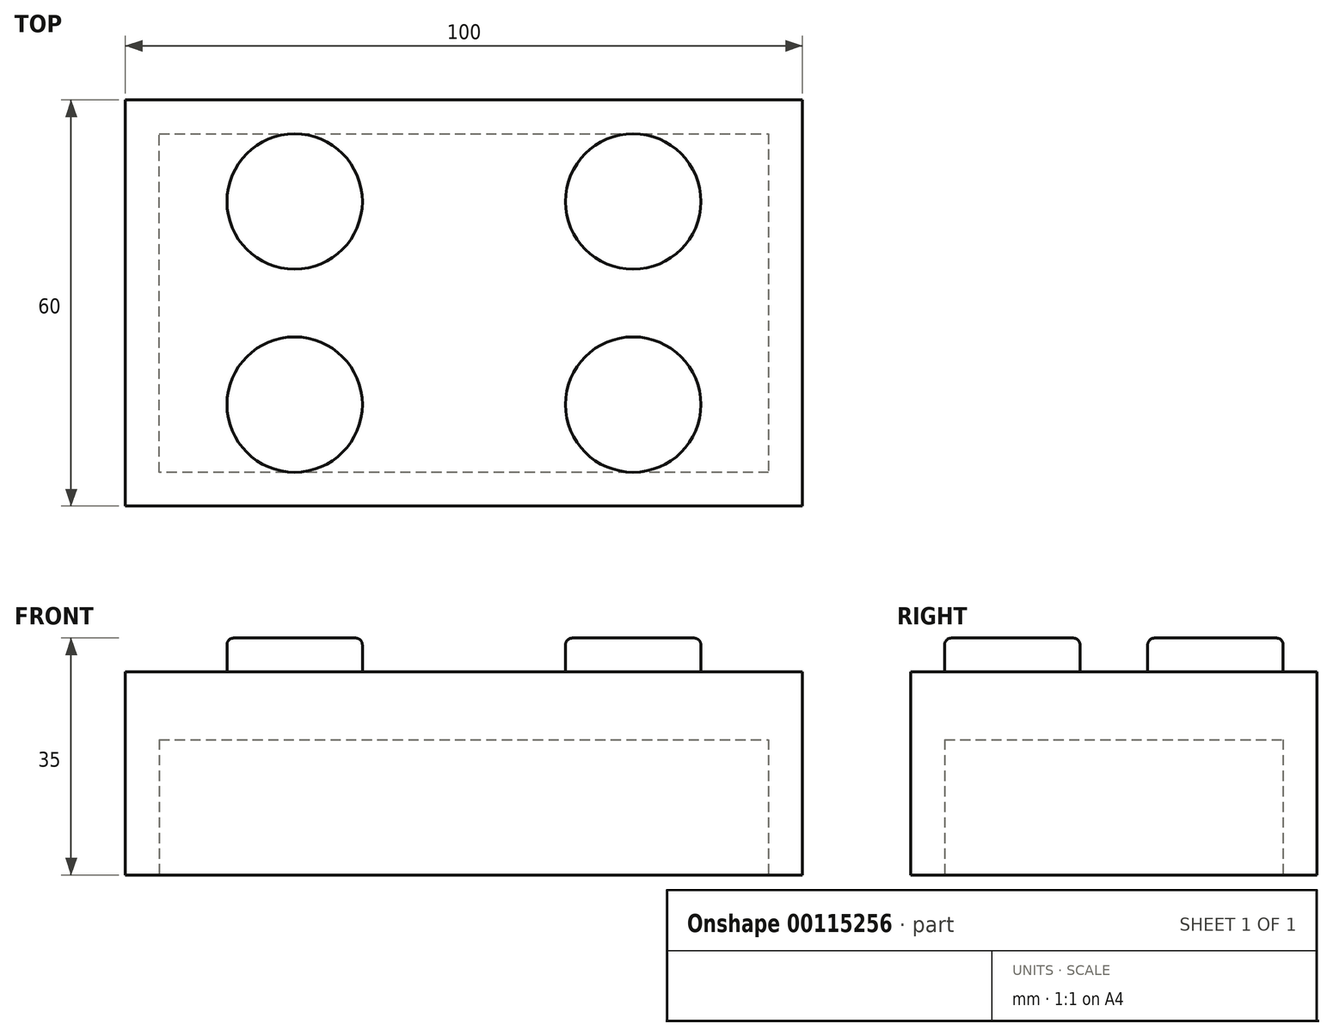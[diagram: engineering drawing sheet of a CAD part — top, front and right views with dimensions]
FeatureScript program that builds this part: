
annotation { "Feature Type Name" : "Feature", "Feature Type Description" : "" }
export const myFeature = defineFeature(function(context is Context, id is Id, definition is map)
    precondition{}
    {
        {
            var Q0;
            Q0=qCreatedBy(makeId("Top.planeOp"),FACE);
            var sketch = newSketch(context, id + "F0", { "sketchPlane" : qUnion([Q0])});
            skLineSegment(sketch, "E0.bottom", {"start": v(-55.04, 76.41) * mm, "end": v(44.96, 76.41) * mm});
            skLineSegment(sketch, "E0.top", {"start": v(-55.04, 16.41) * mm, "end": v(44.96, 16.41) * mm});
            skLineSegment(sketch, "E0.left", {"start": v(-55.04, 76.41) * mm, "end": v(-55.04, 16.41) * mm});
            skLineSegment(sketch, "E0.right", {"start": v(44.96, 76.41) * mm, "end": v(44.96, 16.41) * mm});
            skSolve(sketch);
        }
        {
            var Q0;
            Q0 = qSketchRegion(id + "F0", true);
            extrude(context, id + "F1", {"entities" : qUnion([Q0]), "depth" : 30 * mm});
        }
        {
            var Q0;
            Q0=makeQuery(id+"F1.opExtrude","CAP_FACE",FACE,{"disambiguationData":[OSD([sQuery(id+"F0.wireOp",EDGE,"E0.bottom"),sQuery(id+"F0.wireOp",EDGE,"E0.top"),sQuery(id+"F0.wireOp",EDGE,"E0.left"),sQuery(id+"F0.wireOp",EDGE,"E0.right")])],"isStart":true});
            var sketch = newSketch(context, id + "F2", { "sketchPlane" : qUnion([Q0])});
            skLineSegment(sketch, "E1.0", {"start": v(-50.04, -71.41) * mm, "end": v(39.96, -71.41) * mm});
            skLineSegment(sketch, "E1.1", {"start": v(-50.04, -21.41) * mm, "end": v(-50.04, -71.41) * mm});
            skLineSegment(sketch, "E1.2", {"start": v(39.96, -21.41) * mm, "end": v(-50.04, -21.41) * mm});
            skLineSegment(sketch, "E1.3", {"start": v(39.96, -71.41) * mm, "end": v(39.96, -21.41) * mm});
            skSolve(sketch);
        }
        {
            var Q0;
            Q0=makeQuery(id+"F2.imprint","IMPRINT",FACE,{"disambiguationData":[TD([[makeQuery(id+"F2.imprint","IMPRINT",EDGE,{"derivedFrom":sQuery(id+"F2.wireOp",EDGE,"E1.0")}),1.0]])]});
            extrude(context, id + "F3", {"entities" : qUnion([Q0]), "operationType" : NewBodyOperationType.REMOVE, "oppositeDirection" : true, "depth" : 20 * mm});
        }
        {
            var Q0;
            Q0=makeQuery(id+"F1.opExtrude","CAP_FACE",FACE,{"disambiguationData":[OSD([sQuery(id+"F0.wireOp",EDGE,"E0.bottom"),sQuery(id+"F0.wireOp",EDGE,"E0.top"),sQuery(id+"F0.wireOp",EDGE,"E0.left"),sQuery(id+"F0.wireOp",EDGE,"E0.right")])],"isStart":false});
            var sketch = newSketch(context, id + "F4", { "sketchPlane" : qUnion([Q0])});
            skCircle(sketch, "E2", {"center": v(-30.04, 61.41) * mm, "radius": 10 * mm});
            skCircle(sketch, "E3.0.1.0", {"center": v(-30.04, 31.41) * mm, "radius": 10 * mm});
            skCircle(sketch, "E3.1.0.0", {"center": v(19.96, 61.41) * mm, "radius": 10 * mm});
            skCircle(sketch, "E3.1.1.0", {"center": v(19.96, 31.41) * mm, "radius": 10 * mm});
            skLineSegment(sketch, "E3.direction1", {"start": v(-30.04, 61.41) * mm, "end": v(19.96, 61.41) * mm, "construction": true});
            skLineSegment(sketch, "E3.direction2", {"start": v(-30.04, 61.41) * mm, "end": v(-30.04, 31.41) * mm, "construction": true});
            skSolve(sketch);
        }
        {
            var Q0;
            Q0 = qSketchRegion(id + "F4", true);
            extrude(context, id + "F5", {"entities" : qUnion([Q0]), "operationType" : NewBodyOperationType.ADD, "depth" : 5 * mm});
        }
        {
            var Q0;
            Q0=makeQuery(id+"F5.opExtrude","CAP_EDGE",EDGE,{"disambiguationData":[OSD([sQuery(id+"F4.wireOp",EDGE,"E2")])],"isStart":false});
            var Q1;
            Q1=makeQuery(id+"F5.opExtrude","CAP_EDGE",EDGE,{"disambiguationData":[OSD([sQuery(id+"F4.wireOp",EDGE,"E3.1.0.0")])],"isStart":false});
            var Q2;
            Q2=makeQuery(id+"F5.opExtrude","CAP_EDGE",EDGE,{"disambiguationData":[OSD([sQuery(id+"F4.wireOp",EDGE,"E3.1.1.0")])],"isStart":false});
            var Q3;
            Q3=makeQuery(id+"F5.opExtrude","CAP_EDGE",EDGE,{"disambiguationData":[OSD([sQuery(id+"F4.wireOp",EDGE,"E3.0.1.0")])],"isStart":false});
            fillet(context, id + "F6", {"entities" : qUnion([Q0, Q1, Q2, Q3]), "radius" : 1 * mm, "tangentPropagation" : true, "allowEdgeOverflow" : false});
        }
    });
